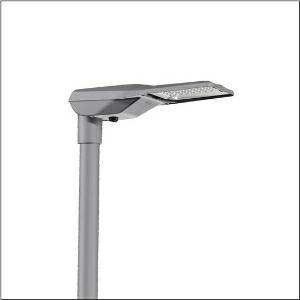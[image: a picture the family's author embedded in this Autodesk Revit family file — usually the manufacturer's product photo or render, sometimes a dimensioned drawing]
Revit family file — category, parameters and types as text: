
# Revit family: streetlight_sl_21_iq_mini___p0_8a_5xe2u31u08hb_1639
name_source: partatom
category: Lighting Fixtures
units: mm (PartAtom-declared; Revit-internal decimal feet)

## family parameters
Cut with Voids When Loaded = No
Host = Face
Light Source = No
Part Type = Normal
Room Calculation Point = No
Round Connector Dimension = Use Diameter
Shared = No

## types (1)
- --- (1 x LED, 9830 lm, 71 W, 3000K)
    Apparent Load = 71 VA
    CIE Flux Codes = 33 69 96 100 100
    Color Rendering = 70
    Color Temperature = 3000K
    Default Elevation = 1800 mm
    Description = Streetlight SL 21 iQ mini, mast luminaire, primary light control with lens, of PMMA, primary optical cover: cover, of toughened safety glass, transparent, light distribution: P0.8a, light emission: direct distribution, primary light characteristic: asymmetric, installation type: post-top, side-entry, LED, High Power LED, rated luminous flux: 9.830lm, luminous efficacy: 139lm/W, light colour: 730, colour temperature: 3000K, control gear: iQ-Street Remote, D4i with power reduction, control: pre-setting: logarithmic dimming characteristic, Street-Remote, Auto-Match, Temp-Guard, Lumen-Switch, Night-Set, Smart-Wire, Light-Fading, Desk-Remote (wireless, voltage-free reading and setting of iQ features in the workshop via application-optimized NFC function/RFID function), optimised constant luminous flux control (CLO 2.0), mains connection: 220..240V, AC, 50/60Hz, start of lifetime: 71W, end of service life: 75W, reduction: 30W, luminaire housing, of diecast aluminium, powder-coated, Siteco® metallic grey (DB 702S), corrosivity category C5 mid according to DIN EN ISO 12944, please order mast flange separately, inclination adjustable: 0°, 5°, 10°, 15°, sealing non-destructively replaceable, multi-level sealing system, length: 628mm, width: 235mm, height: 110mm, mast flange for spigot size: 42mm (side-entry): 5XC10008XM4, 60/48mm (side-entry/post-top): 5XC10108XM2, 76/60mm (side-entry/post-top): 5XC10108XM1, mounting height: 4..8m, Smart Interface below, protection rating (complete): IP66, insulation class (complete): insulation class II (safety insulation), certification: CE, ENEC, ENEC+, VDE, impact resistance: IK10, permissible operating ambient temperature for outdoor applications: -40..+50°C, standard-compliant lighting for roads and squares, packaging unit: 1 piece

Light Distribution: P0.8a
    Height = 110 mm
    Lamp = 1 x LED
    Lamp Light Flux = 9830 lm
    Lamp Power = 71 W
    Lamp count = 1
    Length = 625 mm
    Luminous efficacy = 138 lm/W
    Manufacturer = Siteco
    ModVariant = No
    Model = 5XE2U31U08HB
    Number of Poles = 1
    OnlyDefault = Yes
    Power Factor = 1
    Product Name = Streetlight SL 21 iQ mini | P0.8a
    Product group = mast luminaire | pylon top
    ProductGroupID = 6100
    Protection Class = Protection class II
    Protection Degree = IP 66
    RLX_Detail_Level = 1
    RLX_Emergency_Light_Flux = 0 lm
    RLX_Emergency_Type = 0
    RLX_Emergency_Type_DB = No
    RlxData = <blob elided: 26329 chars, md5=a92cafbb>
    Socket = socket
    Standby Power = 0 W
    System Light Flux = 9830 lm
    System Power = 71 W
    Type Comments = factory setting: luminous flux: 100 % | dim-lin: 254 | 716 mA
    Type Image = l_1003516.jpg
    URL = http://relux.com
    VarID = @adj_074178
    Voltage = 0 V
    Weight = 0.00 kg
    Width = 234 mm

## geometry (parser evidence)
native form markers: Blend x4, Sweep x11
no freeform markers — native parametric forms only
